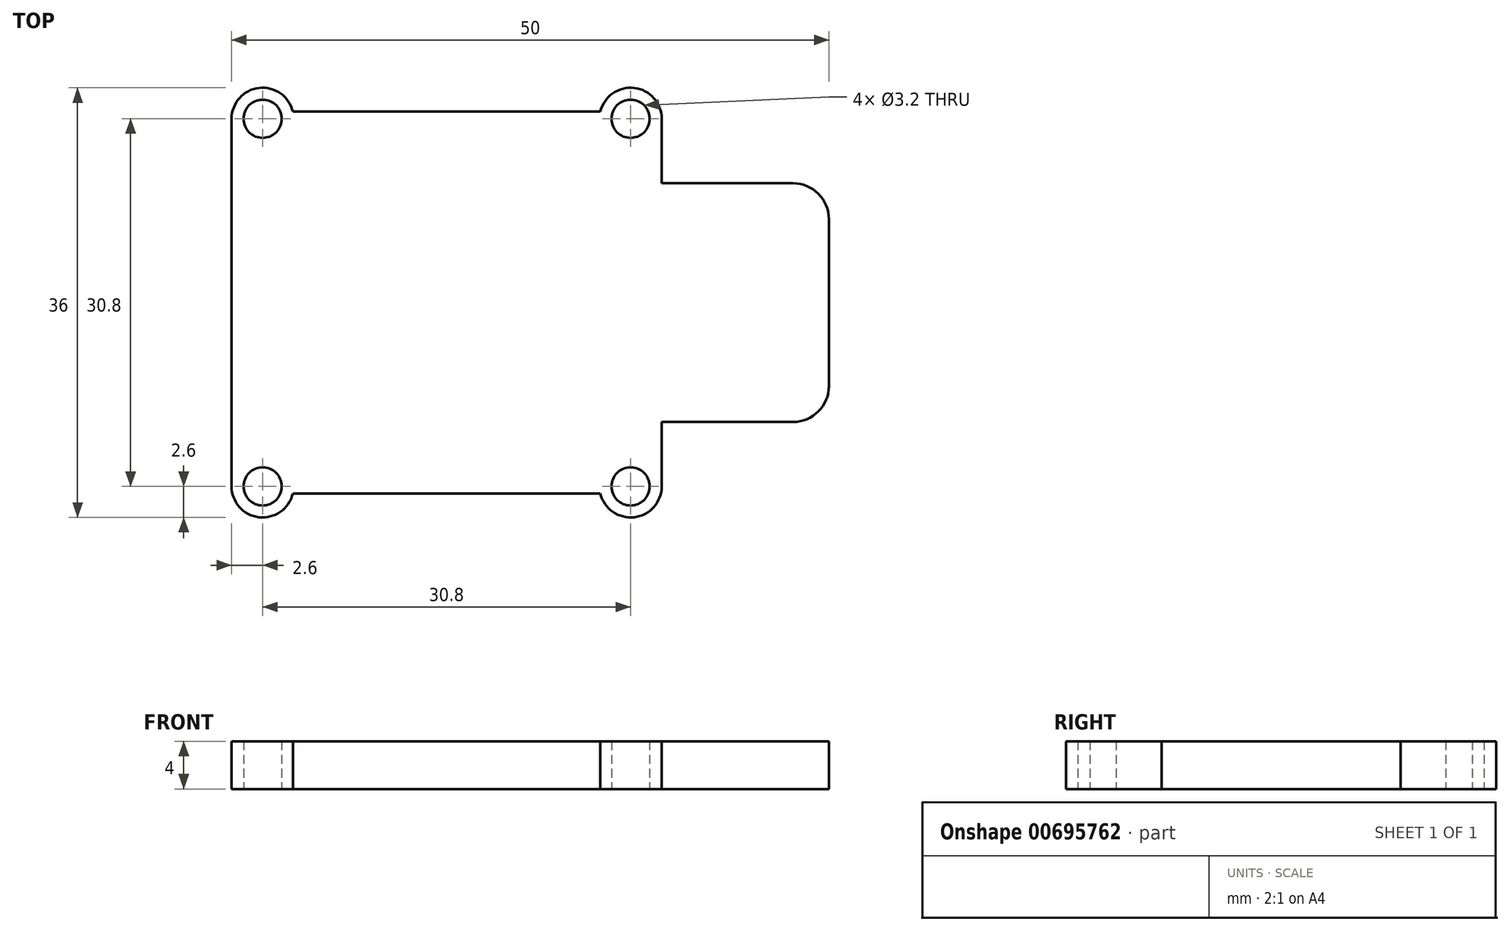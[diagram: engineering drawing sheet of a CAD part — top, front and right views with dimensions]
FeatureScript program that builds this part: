
annotation { "Feature Type Name" : "Feature", "Feature Type Description" : "" }
export const myFeature = defineFeature(function(context is Context, id is Id, definition is map)
    precondition{}
    {
        {
            var Q0;
            Q0=qCreatedBy(makeId("Top.planeOp"),FACE);
            var sketch = newSketch(context, id + "F0", { "sketchPlane" : qUnion([Q0])});
            skLineSegment(sketch, "E0.bottom", {"start": v(18, -18) * mm, "end": v(15.4, -18) * mm, "construction": true});
            skLineSegment(sketch, "E0.top", {"start": v(18, 18) * mm, "end": v(15.4, 18) * mm, "construction": true});
            skLineSegment(sketch, "E0.left", {"start": v(18, -18) * mm, "end": v(18, 18) * mm});
            skLineSegment(sketch, "E0.right", {"start": v(-18, -18) * mm, "end": v(-18, 18) * mm});
            skPoint(sketch, "E0.middle", {"position": v(0, 0) * mm});
            skLineSegment(sketch, "E1.bottom", {"start": v(32, -10) * mm, "end": v(4, -10) * mm});
            skLineSegment(sketch, "E1.top", {"start": v(32, 10) * mm, "end": v(4, 10) * mm});
            skLineSegment(sketch, "E1.left", {"start": v(32, -10) * mm, "end": v(32, 10) * mm});
            skLineSegment(sketch, "E1.right", {"start": v(4, -10) * mm, "end": v(4, 10) * mm});
            skPoint(sketch, "E1.middle", {"position": v(18, 0) * mm});
            skCircle(sketch, "E2", {"center": v(-15.4, 15.4) * mm, "radius": 1.6 * mm});
            skCircle(sketch, "E3.1.0", {"center": v(-15.4, -15.4) * mm, "radius": 1.6 * mm});
            skCircle(sketch, "E3.2.0", {"center": v(15.4, -15.4) * mm, "radius": 1.6 * mm});
            skCircle(sketch, "E3.3.0", {"center": v(15.4, 15.4) * mm, "radius": 1.6 * mm});
            skLineSegment(sketch, "E4.0", {"start": v(18, 16) * mm, "end": v(-18, 16) * mm});
            skLineSegment(sketch, "E5.0", {"start": v(18, -16) * mm, "end": v(-18, -16) * mm});
            skCircle(sketch, "E6", {"center": v(-15.4, 15.4) * mm, "radius": 2.6 * mm});
            skCircle(sketch, "E7", {"center": v(15.4, 15.4) * mm, "radius": 2.6 * mm});
            skCircle(sketch, "E8", {"center": v(15.4, -15.4) * mm, "radius": 2.6 * mm});
            skCircle(sketch, "E9", {"center": v(-15.4, -15.4) * mm, "radius": 2.6 * mm});
            skLineSegment(sketch, "E10.trimOffspring", {"start": v(-15.4, 18) * mm, "end": v(-18, 18) * mm, "construction": true});
            skLineSegment(sketch, "E11.trimOffspring", {"start": v(-15.4, -18) * mm, "end": v(-18, -18) * mm, "construction": true});
            skSolve(sketch);
        }
        {
            var Q0;
            {var subQ14=sQuery(id+"F0.wireOp",EDGE,"E1.right");Q0=makeQuery(id+"F0.imprint","IMPRINT",FACE,{"disambiguationData":[TD([[makeQuery(id+"F0.imprint","IMPRINT",EDGE,{"derivedFrom":subQ14}),1.0]])]});}
            var Q1;
            {var subQ2=sQuery(id+"F0.wireOp",EDGE,"E4.0");var subQ4=sQuery(id+"F0.wireOp",EDGE,"E2");var subQ7=makeQuery(id+"F0.imprint","INTERSECT",VERTEX,{"disambiguationData":[OD(0.0)],"derivedFrom":[subQ4,subQ2]});Q1=makeQuery(id+"F0.imprint","IMPRINT",FACE,{"disambiguationData":[TD([[makeQuery(id+"F0.imprint","IMPRINT",EDGE,{"disambiguationData":[TD([[subQ7,1.0]])],"derivedFrom":subQ4}),-1.0]])]});}
            var Q2;
            {var subQ0=sQuery(id+"F0.wireOp",EDGE,"E4.0");var subQ1=sQuery(id+"F0.wireOp",EDGE,"E2");var subQ2=makeQuery(id+"F0.imprint","INTERSECT",VERTEX,{"disambiguationData":[OD(0.0)],"derivedFrom":[subQ1,subQ0]});Q2=makeQuery(id+"F0.imprint","IMPRINT",FACE,{"disambiguationData":[TD([[makeQuery(id+"F0.imprint","IMPRINT",EDGE,{"disambiguationData":[TD([[subQ2,-1.0]])],"derivedFrom":subQ1}),-1.0]])]});}
            var Q3;
            {var subQ0=sQuery(id+"F0.wireOp",EDGE,"E4.0");var subQ1=sQuery(id+"F0.wireOp",EDGE,"E3.3.0");var subQ2=makeQuery(id+"F0.imprint","INTERSECT",VERTEX,{"disambiguationData":[OD(0.0)],"derivedFrom":[subQ1,subQ0]});Q3=makeQuery(id+"F0.imprint","IMPRINT",FACE,{"disambiguationData":[TD([[makeQuery(id+"F0.imprint","IMPRINT",EDGE,{"disambiguationData":[TD([[subQ2,-1.0]])],"derivedFrom":subQ1}),-1.0]])]});}
            var Q4;
            {var subQ1=sQuery(id+"F0.wireOp",EDGE,"E4.0");var subQ3=sQuery(id+"F0.wireOp",EDGE,"E3.3.0");var subQ7=makeQuery(id+"F0.imprint","INTERSECT",VERTEX,{"disambiguationData":[OD(0.0)],"derivedFrom":[subQ3,subQ1]});Q4=makeQuery(id+"F0.imprint","IMPRINT",FACE,{"disambiguationData":[TD([[makeQuery(id+"F0.imprint","IMPRINT",EDGE,{"disambiguationData":[TD([[subQ7,1.0]])],"derivedFrom":subQ3}),-1.0]])]});}
            var Q5;
            {var subQ0=sQuery(id+"F0.wireOp",EDGE,"E5.0");var subQ1=sQuery(id+"F0.wireOp",EDGE,"E3.2.0");var subQ2=makeQuery(id+"F0.imprint","INTERSECT",VERTEX,{"disambiguationData":[OD(0.0)],"derivedFrom":[subQ1,subQ0]});Q5=makeQuery(id+"F0.imprint","IMPRINT",FACE,{"disambiguationData":[TD([[makeQuery(id+"F0.imprint","IMPRINT",EDGE,{"disambiguationData":[TD([[subQ2,1.0]])],"derivedFrom":subQ1}),-1.0]])]});}
            var Q6;
            {var subQ2=sQuery(id+"F0.wireOp",EDGE,"E5.0");var subQ5=sQuery(id+"F0.wireOp",EDGE,"E3.2.0");var subQ6=makeQuery(id+"F0.imprint","INTERSECT",VERTEX,{"disambiguationData":[OD(0.0)],"derivedFrom":[subQ5,subQ2]});Q6=makeQuery(id+"F0.imprint","IMPRINT",FACE,{"disambiguationData":[TD([[makeQuery(id+"F0.imprint","IMPRINT",EDGE,{"disambiguationData":[TD([[subQ6,-1.0]])],"derivedFrom":subQ5}),-1.0]])]});}
            var Q7;
            {var subQ2=sQuery(id+"F0.wireOp",EDGE,"E5.0");var subQ4=sQuery(id+"F0.wireOp",EDGE,"E3.1.0");var subQ7=makeQuery(id+"F0.imprint","INTERSECT",VERTEX,{"disambiguationData":[OD(0.0)],"derivedFrom":[subQ4,subQ2]});Q7=makeQuery(id+"F0.imprint","IMPRINT",FACE,{"disambiguationData":[TD([[makeQuery(id+"F0.imprint","IMPRINT",EDGE,{"disambiguationData":[TD([[subQ7,-1.0]])],"derivedFrom":subQ4}),-1.0]])]});}
            var Q8;
            {var subQ0=sQuery(id+"F0.wireOp",EDGE,"E5.0");var subQ1=sQuery(id+"F0.wireOp",EDGE,"E3.1.0");var subQ2=makeQuery(id+"F0.imprint","INTERSECT",VERTEX,{"disambiguationData":[OD(0.0)],"derivedFrom":[subQ1,subQ0]});Q8=makeQuery(id+"F0.imprint","IMPRINT",FACE,{"disambiguationData":[TD([[makeQuery(id+"F0.imprint","IMPRINT",EDGE,{"disambiguationData":[TD([[subQ2,1.0]])],"derivedFrom":subQ1}),-1.0]])]});}
            var Q9;
            {var subQ5=sQuery(id+"F0.wireOp",EDGE,"E1.right");Q9=makeQuery(id+"F0.imprint","IMPRINT",FACE,{"disambiguationData":[TD([[makeQuery(id+"F0.imprint","IMPRINT",EDGE,{"derivedFrom":subQ5}),-1.0]])]});}
            var Q10;
            {var subQ5=sQuery(id+"F0.wireOp",EDGE,"E1.left");Q10=makeQuery(id+"F0.imprint","IMPRINT",FACE,{"disambiguationData":[TD([[makeQuery(id+"F0.imprint","IMPRINT",EDGE,{"derivedFrom":subQ5}),1.0]])]});}
            extrude(context, id + "F1", {"entities" : qUnion([Q0, Q1, Q2, Q3, Q4, Q5, Q6, Q7, Q8, Q9, Q10]), "depth" : 4 * mm, "offsetDistance" : 25 * mm});
        }
        {
            var Q0;
            Q0=makeQuery(id+"F1.opExtrude","SWEPT_EDGE",EDGE,{"disambiguationData":[OSD([sQuery(id+"F0.wireOp",EDGE,"E1.top"),sQuery(id+"F0.wireOp",EDGE,"E1.left")])]});
            var Q1;
            Q1=makeQuery(id+"F1.opExtrude","SWEPT_EDGE",EDGE,{"disambiguationData":[OSD([sQuery(id+"F0.wireOp",EDGE,"E1.bottom"),sQuery(id+"F0.wireOp",EDGE,"E1.left")])]});
            fillet(context, id + "F2", {"entities" : qUnion([Q0, Q1]), "radius" : 3 * mm, "tangentPropagation" : true, "allowEdgeOverflow" : false});
        }
    });
